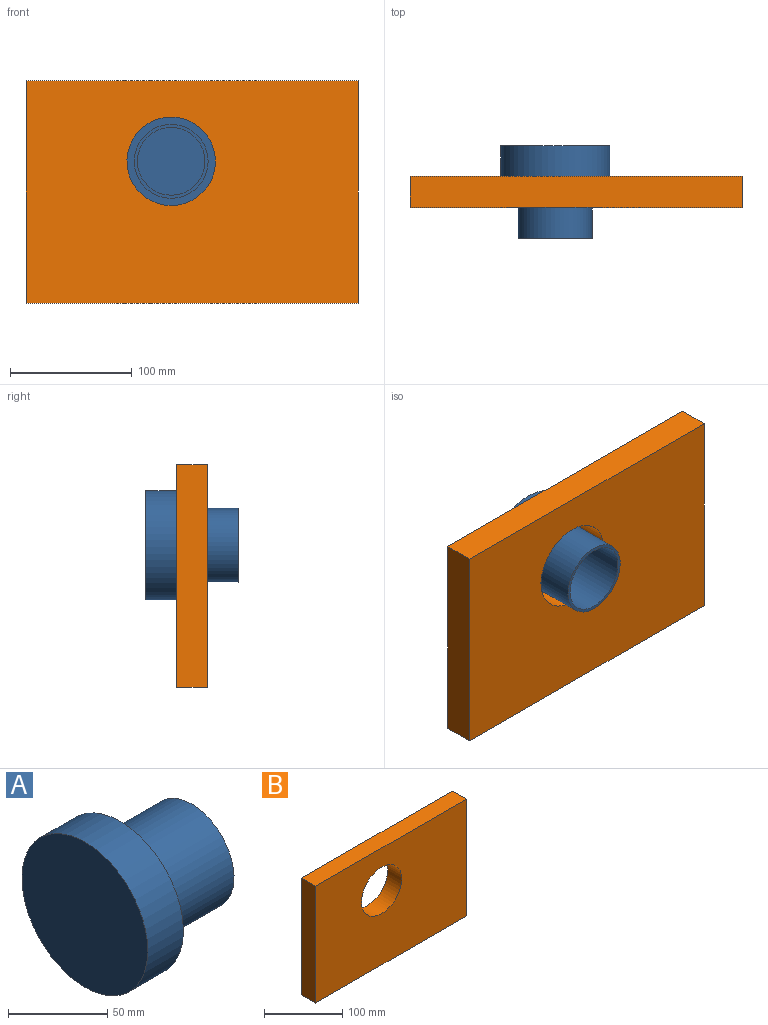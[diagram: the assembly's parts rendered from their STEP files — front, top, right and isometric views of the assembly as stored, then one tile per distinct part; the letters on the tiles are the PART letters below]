
ASSEMBLY  parts=2 mates=1
PART A: 7 faces, bbox 76.2x89.8x89.8 mm
  f0: cylinder r=30.32mm len=60.63mm, axis (-1,0,0), area 9676.8mm2, adj f1,f6
  f1: plane 60.63x60.63mm, normal (1,0,0), area 463.6mm2, adj f0,f2
  f2: cylinder r=27.78mm len=55.55mm, axis (-1,0,0), area 8422.8mm2, adj f1,f3
  f3: plane 55.55x55.55mm, normal (1,0,0), area 2424mm2, adj f2
  f4: cylinder r=44.91mm len=89.82mm, axis (1,0,0), area 7167.5mm2, adj f5,f6
  f5: plane 89.82x89.82mm, normal (-1,0,0), area 6336.7mm2, adj f4
  f6: plane 89.82x89.82mm, normal (1,0,0), area 3449.2mm2, adj f0,f4
PART B: 7 faces, bbox 272.7x25.4x182.9 mm
  f0: plane 182.89x25.4mm, normal (-1,0,0), area 4645.3mm2, adj f1,f3,f5,f6
  f1: plane 272.72x25.4mm, normal (0,0,-1), area 6927.1mm2, adj f0,f2,f5,f6
  f2: plane 182.89x25.4mm, normal (1,0,0), area 4645.3mm2, adj f1,f3,f5,f6
  f3: plane 272.72x25.4mm, normal (0,0,1), area 6927.1mm2, adj f0,f2,f5,f6
  f4: cylinder r=36.32mm len=72.63mm, axis (0,1,0), area 5795.9mm2, adj f5,f6
  f5: plane 272.72x182.89mm, normal (0,-1,0), area 45733.7mm2, adj f0,f1,f2,f3,f4
  f6: plane 272.72x182.89mm, normal (0,1,0), area 45733.7mm2, adj f0,f1,f2,f3,f4
PLACE A rot(axis=(0.71,-0.71,0),180deg) t=(-109.65,-89.6,-119.89)mm
PLACE B t=(-53.32,-89.6,-144.79)mm
MATE fastened A.f4 <-> B.f4  axis (0,-1,0) through (-109.65,-89.6,-119.89)mm
